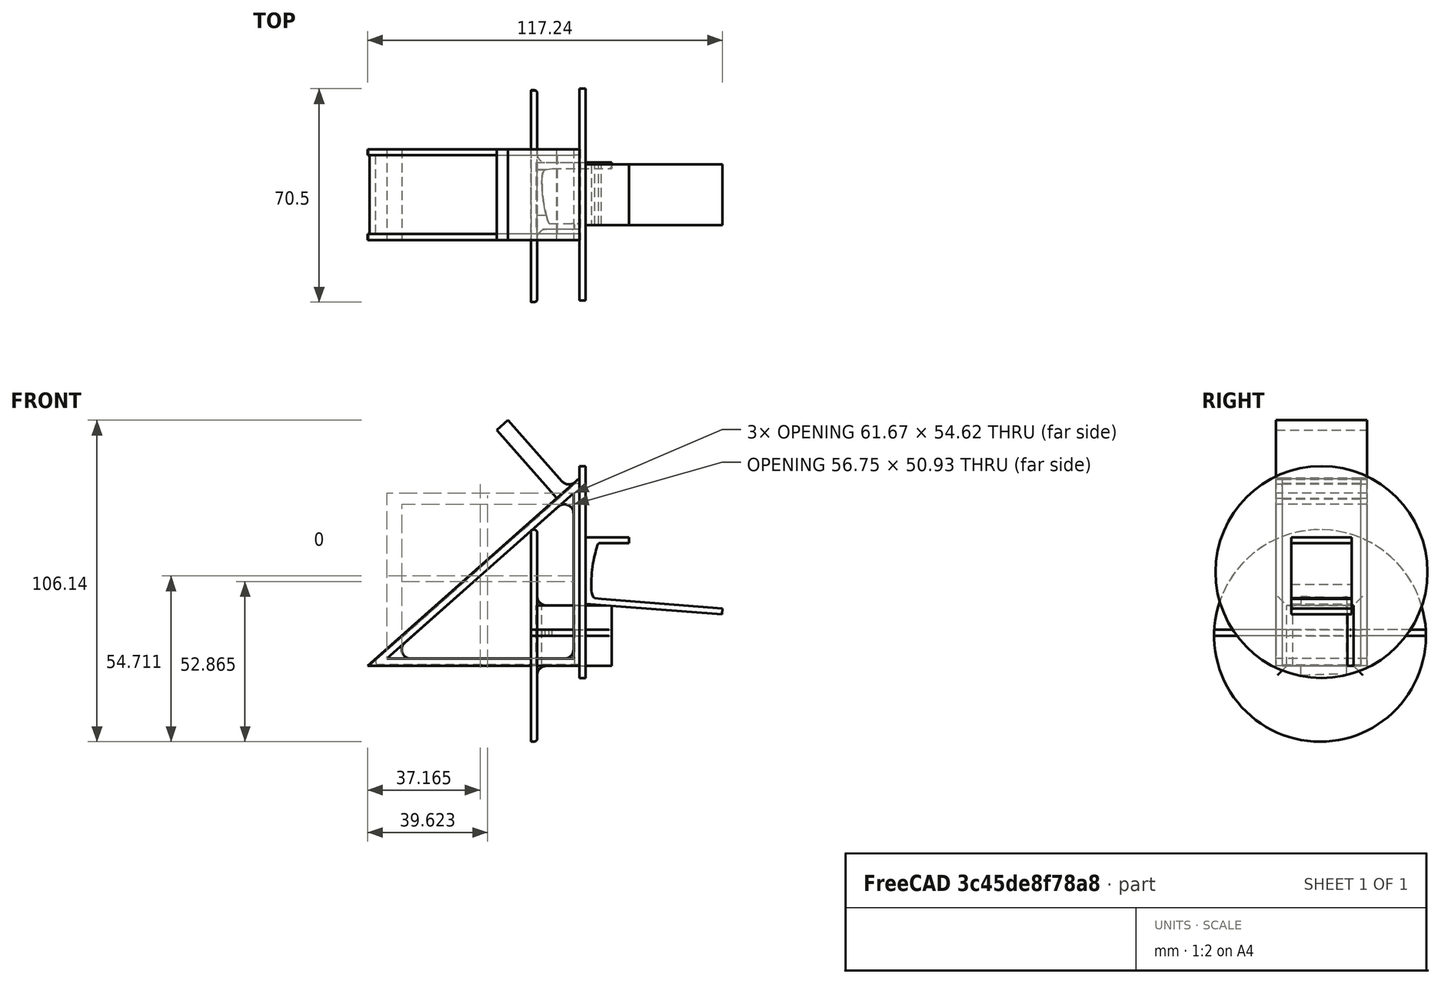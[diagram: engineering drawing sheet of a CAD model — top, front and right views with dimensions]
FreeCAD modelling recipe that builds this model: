
FCSTD DOCUMENT  (FreeCAD 0.20R29603 (Git))
Label: soporte
License: All rights reserved
LicenseURL: http://en.wikipedia.org/wiki/All_rights_reserved
objects: Sketcher::SketchObject×11, PartDesign::Body×8, PartDesign::Pad×6, PartDesign::Fillet×6, Mesh::Feature×4, Part::Feature×3, Part::Box×3, Part::Cut×3, Part::Fillet×3, Part::MultiFuse×3, PartDesign::Pocket×3, Part::Cylinder×2, Image::ImagePlane×1
note: 66 computed .brp shape members not serialized (recipe doc carries the construction recipe); baked Part::Feature solids carry a one-line shape summary decoded from their .brp

FEATURE [Image::ImagePlane] ImagePlane
  Placement = pos=(0,0,0) rot=(0,0,1;-0.034907rad)
  XSize = 116.767
  YSize = 87.5751
FEATURE [Sketcher::SketchObject] Sketch
  FullyConstrained = false
  MapMode = 5
  Support = -> [XY_Plane]
  sketch-geometry (21):
    g0: LineSegment StartX=-10 StartY=-9.49 StartZ=0 EndX=0 EndY=-9.49 EndZ=0
    g1: LineSegment StartX=0 StartY=-11.49 StartZ=0 EndX=-14.4197 EndY=-11.49 EndZ=0
    g2: LineSegment StartX=-11.2797 StartY=8.28 StartZ=0 EndX=-9.03969 EndY=8.58 EndZ=0
    g3: LineSegment StartX=-9.03969 StartY=8.58 StartZ=0 EndX=10.5803 EndY=8.58 EndZ=0
    g4-g10: Circle x7 (B-spline internal-alignment scaffolding for g11; pole/knot coordinates omitted)
    g11: BSplineCurve PolesCount=7 KnotsCount=5 Degree=3 IsPeriodic=0
    g12-g16: GeomPoint x5 (B-spline internal-alignment scaffolding for g11; pole/knot coordinates omitted)
    g17: LineSegment StartX=-14.4197 StartY=10.58 StartZ=0 EndX=-14.4197 EndY=-11.49 EndZ=0
    g18: LineSegment StartX=-14.4197 StartY=10.58 StartZ=0 EndX=10.5803 EndY=10.58 EndZ=0
    g19: LineSegment StartX=10.5803 StartY=10.58 StartZ=0 EndX=10.5803 EndY=8.58 EndZ=0
    g20: LineSegment StartX=0 StartY=-9.49 StartZ=0 EndX=0 EndY=-11.49 EndZ=0
  constraints (25):
    c: PointOnObject(g0,g-2)
    c: Horizontal(g0)
    c: PointOnObject(g1,g-2)
    c: Horizontal(g3)
    c: Coincident(g11,g2)
    c: Equal(g4, g5-g10) x6
    c: Coincident(g11,g0)
    c: InternalAlignment(g4-g10 -> g11) x7
    c: InternalAlignment(g12-g16 -> g11) x5
    c: DistanceY(g3,g18) = 2
    c: Coincident(g3,g2)
    c: DistanceX(g0,g0) = 10
    c: DistanceX(g17,g13) = 2
    c: Vertical(g17)
    c: Coincident(g1,g17)
    c: Coincident(g18,g17)
    c: Horizontal(g18)
    c: Horizontal(g1)
    c: DistanceY(g2,g2) = 0.3
    c: DistanceX(g3,g3) = 19.62
    c: DistanceX(g2,g2) = 2.24
    c: Coincident(g3,g19)
    c: Vertical(g20)
    c: Coincident(g20,g1)
    c: DistanceY(g20,g20) = 2
FEATURE [PartDesign::Pad] Pad
  Direction = (0,0,1)
  Length = 20
  Length2 = 10
  Profile = -> Sketch
  ReferenceAxis = -> Sketch [N_Axis]
  Type = 0
FEATURE [PartDesign::Body] Body
  Group = -> [Sketch,Pad]
  Origin = -> Origin
  Tip = -> Pad
FEATURE [Part::Feature] Body001
  shape: bbox 25 x 22.07 x 20 mm, 11 faces (baked)
FEATURE [Part::Box] Box  label="Cube"
  AttacherType = Attacher::AttachEngine3D
  Height = 21
  Length = 10
  Placement = pos=(-1.5,-16,0) rot=(0,0,1;0rad)
  Width = 12
FEATURE [Part::Cut] Cut
  Base = -> Body001
  Tool = -> Box
FEATURE [Part::Fillet] Fillet
  Base = -> Cut
  Edges = 4 edges r=0.9: [Edge9,Edge23,Edge24,Edge27]
FEATURE [Part::Cylinder] Cylinder
  Angle = 360
  AttacherType = Attacher::AttachEngine3D
  FirstAngle = 0
  Height = 2
  Placement = pos=(-16,-0.5,10) rot=(0,1,0;1.5708rad)
  Radius = 35
  SecondAngle = 0
FEATURE [Part::MultiFuse] Fusion
  Shapes = -> [Fillet,Cylinder]
FEATURE [Part::Fillet] Fillet001
  Base = -> Fusion
  Edges = 1 edges r=1: [Edge3]
FEATURE [Part::Fillet] Fillet002  label="pieza_tv"
  Base = -> Fillet001
  Edges = 4 edges r=3: [Edge6,Edge7,Edge8,Edge9]
FEATURE [Part::Feature] Fillet002001
  shape: bbox 26.58 x 75.77 x 75.77 mm, 30 faces (baked)
FEATURE [Part::Box] Box001  label="Cube001"
  AttacherType = Attacher::AttachEngine3D
  Height = 38
  Length = 42
  Placement = pos=(-21,-39,12) rot=(0,0,1;0rad)
  Width = 89
FEATURE [Part::Box] Box002  label="Cube002"
  AttacherType = Attacher::AttachEngine3D
  Height = 38
  Length = 42
  Placement = pos=(-21,-39,-28) rot=(0,0,1;0rad)
  Width = 89
FEATURE [Part::Cut] Cut001
  Base = -> Fillet002001
  Tool = -> Box001
FEATURE [Part::Cut] Cut002  label="prueba"
  Base = -> Cut001
  Tool = -> Box002
FEATURE [Mesh::Feature] Mesh  label="pieza"
FEATURE [Mesh::Feature] Mesh001  label="prueba001"
FEATURE [Sketcher::SketchObject] Sketch001
  FullyConstrained = true
  MapMode = 5
  Support = -> [XY_Plane001]
  sketch-geometry (1):
    g0: Circle CenterX=0 CenterY=0 CenterZ=0 NormalX=0 NormalY=0 NormalZ=1 AngleXU=0 Radius=15.5
  constraints (2):
    c: Coincident(g0,g-1)
    c: Diameter(g0) = 31
FEATURE [PartDesign::Body] Body002
  Group = -> [Sketch001]
  Origin = -> Origin001
FEATURE [PartDesign::Body] Body003
  Origin = -> Origin002
FEATURE [Sketcher::SketchObject] Sketch002
  FullyConstrained = false
  MapMode = 5
  Placement = pos=(0,0,0) rot=(1,0,0;1.5708rad)
  Support = -> [XZ_Plane003]
  sketch-geometry (7):
    g0: LineSegment StartX=0 StartY=0 StartZ=0 EndX=-70 EndY=0 EndZ=0
    g1: LineSegment StartX=-70 StartY=0 StartZ=0 EndX=0 EndY=62 EndZ=0
    g2: LineSegment StartX=0 StartY=62 StartZ=0 EndX=0 EndY=0 EndZ=0
    g3: LineSegment StartX=-2 StartY=2.4 StartZ=0 EndX=-63.6706 EndY=2.4 EndZ=0
    g4: LineSegment StartX=-63.6706 StartY=2.4 StartZ=0 EndX=-2 EndY=57.0225 EndZ=0
    g5: LineSegment StartX=-2 StartY=57.0225 StartZ=0 EndX=-2 EndY=2.4 EndZ=0
    g6: LineSegment StartX=-29.563 StartY=35.8157 StartZ=0 EndX=-27.9717 EndY=34.0191 EndZ=0
  constraints (20):
    c: Coincident(g-1,g0)
    c: PointOnObject(g0,g-1)
    c: Coincident(g0,g1)
    c: Coincident(g1,g2)
    c: Coincident(g2,g0)
    c: Vertical(g2)
    c: DistanceX(g0,g0) = 70
    c: DistanceY(g2,g2) = 62
    c: Horizontal(g3)
    c: Coincident(g3,g4)
    c: Coincident(g4,g5)
    c: Coincident(g5,g3)
    c: Vertical(g5)
    c: DistanceX(g3,g0) = 2
    c: DistanceY(g0,g3) = 2.4
    c: PointOnObject(g6,g1)
    c: Parallel(g1,g4)
    c: Perpendicular(g6,g1)
    c: PointOnObject(g6,g4)
    c: Distance(g6) = 2.4
FEATURE [PartDesign::Pad] Pad001
  Direction = (0,-1,2e-16)
  Length = 30
  Length2 = 10
  Midplane = true
  Placement = pos=(0,0,0) rot=(1,0,0;1.5708rad)
  Profile = -> Sketch002
  ReferenceAxis = -> Sketch002 [N_Axis]
  Type = 0
FEATURE [Sketcher::SketchObject] Sketch003
  ExternalGeometry = -> [Pad001]
  FullyConstrained = true
  MapMode = 5
  Placement = pos=(-30.7731,2.3e-14,34.7438) rot=(-0.35455,0,0.935037;3.14159rad)
  Support = -> [Pad001]
  sketch-geometry (4):
    g0: LineSegment StartX=-41.1082 StartY=13 StartZ=0 EndX=52.4012 EndY=13 EndZ=0
    g1: LineSegment StartX=52.4012 StartY=13 StartZ=0 EndX=52.4012 EndY=-13 EndZ=0
    g2: LineSegment StartX=52.4012 StartY=-13 StartZ=0 EndX=-41.1082 EndY=-13 EndZ=0
    g3: LineSegment StartX=-41.1082 StartY=-13 StartZ=0 EndX=-41.1082 EndY=13 EndZ=0
  constraints (11):
    c: Coincident(g0,g1)
    c: Coincident(g1,g2)
    c: Coincident(g2,g3)
    c: Coincident(g3,g0)
    c: Horizontal(g0)
    c: Horizontal(g2)
    c: Vertical(g1)
    c: Symmetric(g0,g2,g-1)
    c: DistanceY(g3,g3) = 26
    c: PointOnObject(g2,g-3)
    c: PointOnObject(g0,g-4)
FEATURE [PartDesign::Pocket] Pocket
  BaseFeature = -> Pad001
  Direction = (0.663035,-2e-16,-0.748588)
  Length = 0.37
  Length2 = 5
  Placement = pos=(0,0,0) rot=(1,0,0;1.5708rad)
  Profile = -> Sketch003
  ReferenceAxis = -> Sketch003 [N_Axis]
  Type = 0
FEATURE [Sketcher::SketchObject] Sketch004
  ExternalGeometry = -> [Pocket]
  FullyConstrained = true
  MapMode = 5
  Placement = pos=(0,0,-1e-16) rot=(1,0,0;3.14159rad)
  Support = -> [Pocket]
  sketch-geometry (4):
    g0: LineSegment StartX=-69.442 StartY=13 StartZ=0 EndX=0 EndY=13 EndZ=0
    g1: LineSegment StartX=0 StartY=13 StartZ=0 EndX=0 EndY=-13 EndZ=0
    g2: LineSegment StartX=0 StartY=-13 StartZ=0 EndX=-69.442 EndY=-13 EndZ=0
    g3: LineSegment StartX=-69.442 StartY=-13 StartZ=0 EndX=-69.442 EndY=13 EndZ=0
  constraints (10):
    c: Coincident(g0,g1)
    c: Coincident(g1,g2)
    c: Coincident(g2,g3)
    c: Coincident(g3,g0)
    c: Horizontal(g0)
    c: Horizontal(g2)
    c: Vertical(g1)
    c: Symmetric(g0,g2,g-1)
    c: Coincident(g0,g-4)
    c: PointOnObject(g0,g-2)
FEATURE [PartDesign::Pocket] Pocket001
  BaseFeature = -> Pocket
  Direction = (0,2e-16,1)
  Length = 0.37
  Length2 = 5
  Placement = pos=(0,0,0) rot=(1,0,0;1.5708rad)
  Profile = -> Sketch004
  ReferenceAxis = -> Sketch004 [N_Axis]
  Type = 0
FEATURE [PartDesign::Fillet] Fillet002002
  Base = -> Pocket001 [Edge27,Edge30,Edge28]
  BaseFeature = -> Pocket001
  Placement = pos=(0,0,0) rot=(1,0,0;1.5708rad)
  Radius = 3
  SupportTransform = false
  UseAllEdges = false
FEATURE [PartDesign::Fillet] Fillet002003
  Base = -> Fillet002002 [Edge26,Edge33]
  BaseFeature = -> Fillet002002
  Placement = pos=(0,0,0) rot=(1,0,0;1.5708rad)
  Radius = 0.2
  SupportTransform = false
  UseAllEdges = false
FEATURE [PartDesign::Fillet] Fillet002004
  Base = -> Fillet002003 [Edge21]
  BaseFeature = -> Fillet002003
  Placement = pos=(0,0,0) rot=(1,0,0;1.5708rad)
  Radius = 1
  SupportTransform = false
  UseAllEdges = false
FEATURE [PartDesign::Fillet] Fillet002005
  Base = -> Fillet002004 [Edge57,Edge40]
  BaseFeature = -> Fillet002004
  Placement = pos=(0,0,0) rot=(1,0,0;1.5708rad)
  Radius = 0.2
  SupportTransform = false
  UseAllEdges = false
FEATURE [PartDesign::Fillet] Fillet002006
  Base = -> Fillet002005 [Edge24]
  BaseFeature = -> Fillet002005
  Placement = pos=(0,0,0) rot=(1,0,0;1.5708rad)
  Radius = 1
  SupportTransform = false
  UseAllEdges = false
FEATURE [PartDesign::Body] Body004  label="triangulo"
  Group = -> [Sketch002,Pad001,Sketch003,Pocket,Sketch004,Pocket001,Fillet002002,Fillet002003,Fillet002004,Fillet002005,Fillet002006]
  Origin = -> Origin003
  Tip = -> Fillet002006
FEATURE [Mesh::Feature] Mesh002  label="triangulo001"
FEATURE [Part::Cylinder] Cylinder001  label="cilindro_grande"
  Angle = 360
  AttacherType = Attacher::AttachEngine3D
  FirstAngle = 0
  Height = 2
  Placement = pos=(-16.3,0,0) rot=(0,1,0;1.5708rad)
  Radius = 35
  SecondAngle = 0
FEATURE [Sketcher::SketchObject] Sketch005
  FullyConstrained = false
  MapMode = 5
  Support = -> [XY_Plane004]
  sketch-geometry (21):
    g0: LineSegment StartX=-10 StartY=-9.49 StartZ=0 EndX=0 EndY=-9.49 EndZ=0
    g1: LineSegment StartX=0 StartY=-11.49 StartZ=0 EndX=-14.42 EndY=-11.49 EndZ=0
    g2: LineSegment StartX=-11.28 StartY=8.59 StartZ=0 EndX=-9.04 EndY=8.89 EndZ=0
    g3: LineSegment StartX=-9.04 StartY=8.89 StartZ=0 EndX=30.9357 EndY=11.98 EndZ=0
    g4-g10: Circle x7 (B-spline internal-alignment scaffolding for g11; pole/knot coordinates omitted)
    g11: BSplineCurve PolesCount=7 KnotsCount=5 Degree=3 IsPeriodic=0
    g12-g16: GeomPoint x5 (B-spline internal-alignment scaffolding for g11; pole/knot coordinates omitted)
    g17: LineSegment StartX=-14.25 StartY=10.48 StartZ=0 EndX=-14.42 EndY=-11.49 EndZ=0
    g18: LineSegment StartX=-14.25 StartY=10.48 StartZ=0 EndX=30.7826 EndY=13.9609 EndZ=0
    g19: LineSegment StartX=0 StartY=-9.49 StartZ=0 EndX=0 EndY=-11.49 EndZ=0
    g20: LineSegment StartX=30.9357 StartY=11.98 StartZ=0 EndX=30.7826 EndY=13.9609 EndZ=0
  constraints (30):
    c: PointOnObject(g0,g-2)
    c: Horizontal(g0)
    c: PointOnObject(g1,g-2)
    c: Coincident(g11,g2)
    c: Equal(g4, g5-g10) x6
    c: Coincident(g11,g0)
    c: InternalAlignment(g4-g10 -> g11) x7
    c: InternalAlignment(g12-g16 -> g11) x5
    c: Horizontal(g1)
    c: Vertical(g19)
    c: Coincident(g19,g1)
    c: Parallel(g3,g18)
    c: DistanceY(g1,g0) = 2
    c: DistanceX(g0,g-1) = 10
    c: DistanceX(g1,g1) = 14.42
    c: DistanceY(g17,g17) = 21.97
    c: DistanceY(g-1,g2) = 8.89
    c: DistanceX(g2,g-1) = 9.04
    c: DistanceX(g2,g-1) = 11.28
    c: Coincident(g2,g3)
    c: Coincident(g17,g18)
    c: DistanceY(g-1,g17) = 10.48
    c: DistanceY(g-1,g2) = 8.59
    c: DistanceY(g-1,g3) = 11.98
    c: Angle(g18) = 0.0771436
    c: DistanceX(g17,g-1) = 14.25
    c: Coincident(g1,g17)
    c: Coincident(g3,g20)
    c: Perpendicular(g3,g20)
    c: Coincident(g18,g20)
FEATURE [PartDesign::Pad] Pad002
  Direction = (0,0,1)
  Length = 20
  Length2 = 10
  Midplane = true
  Profile = -> Sketch005
  ReferenceAxis = -> Sketch005 [N_Axis]
  Type = 0
FEATURE [PartDesign::Body] Body005  label="soporte_grande"
  Group = -> [Sketch005,Pad002]
  Origin = -> Origin004
  Tip = -> Pad002
FEATURE [Mesh::Feature] Mesh003  label="soporte_grande_test"
FEATURE [Sketcher::SketchObject] Sketch006
  ExternalGeometry = -> [Pad002]
  FullyConstrained = false
  MapMode = 5
  Placement = pos=(-14.3302,0.110885,0) rot=(-0.574372,0.578834,0.578834;4.18432rad)
  Support = -> [Pad002]
  sketch-geometry (2):
    g0: LineSegment StartX=-10.3694 StartY=10 StartZ=0 EndX=11.4689 EndY=-10 EndZ=0
    g1: LineSegment StartX=11.6012 StartY=9.89041 StartZ=0 EndX=-10.3694 EndY=-9.89756 EndZ=0
  constraints (4):
    c: Coincident(g0,g-4)
    c: PointOnObject(g0,g-6)
    c: PointOnObject(g1,g-5)
    c: PointOnObject(g1,g-4)
FEATURE [PartDesign::Body] Body006  label="triangulo002"
  Origin = -> Origin005
  Placement = pos=(-16.3,0,-31) rot=(0,0,1;0rad)
FEATURE [Sketcher::SketchObject] Sketch007
  FullyConstrained = false
  MapMode = 5
  Placement = pos=(0,0,0) rot=(1,0,0;1.5708rad)
  Support = -> [XZ_Plane005]
  sketch-geometry (7):
    g0: LineSegment StartX=0 StartY=0 StartZ=0 EndX=-70 EndY=0 EndZ=0
    g1: LineSegment StartX=-70 StartY=0 StartZ=0 EndX=0 EndY=62 EndZ=0
    g2: LineSegment StartX=0 StartY=62 StartZ=0 EndX=0 EndY=0 EndZ=0
    g3: LineSegment StartX=-2 StartY=2.4 StartZ=0 EndX=-63.6706 EndY=2.4 EndZ=0
    g4: LineSegment StartX=-63.6706 StartY=2.4 StartZ=0 EndX=-2 EndY=57.0225 EndZ=0
    g5: LineSegment StartX=-2 StartY=57.0225 StartZ=0 EndX=-2 EndY=2.4 EndZ=0
    g6: LineSegment StartX=-29.563 StartY=35.8157 StartZ=0 EndX=-27.9717 EndY=34.0191 EndZ=0
  constraints (20):
    c: Coincident(g-1,g0)
    c: PointOnObject(g0,g-1)
    c: Coincident(g0,g1)
    c: Coincident(g1,g2)
    c: Coincident(g2,g0)
    c: Vertical(g2)
    c: DistanceX(g0,g0) = 70
    c: DistanceY(g2,g2) = 62
    c: Horizontal(g3)
    c: Coincident(g3,g4)
    c: Coincident(g4,g5)
    c: Coincident(g5,g3)
    c: Vertical(g5)
    c: DistanceX(g3,g0) = 2
    c: DistanceY(g0,g3) = 2.4
    c: PointOnObject(g6,g1)
    c: Parallel(g1,g4)
    c: Perpendicular(g6,g1)
    c: PointOnObject(g6,g4)
    c: Distance(g6) = 2.4
FEATURE [PartDesign::Pad] Pad003
  Direction = (0,-1,2e-16)
  Length = 30
  Length2 = 10
  Midplane = true
  Placement = pos=(0,0,0) rot=(1,0,0;1.5708rad)
  Profile = -> Sketch007
  ReferenceAxis = -> Sketch007 [N_Axis]
  Type = 0
FEATURE [Sketcher::SketchObject] Sketch008
  ExternalGeometry = -> [Pad003]
  FullyConstrained = true
  MapMode = 5
  Placement = pos=(-30.7731,2.3e-14,34.7438) rot=(-0.35455,0,0.935037;3.14159rad)
  Support = -> [Pad003]
  sketch-geometry (4):
    g0: LineSegment StartX=-41.1082 StartY=13 StartZ=0 EndX=52.4012 EndY=13 EndZ=0
    g1: LineSegment StartX=52.4012 StartY=13 StartZ=0 EndX=52.4012 EndY=-13 EndZ=0
    g2: LineSegment StartX=52.4012 StartY=-13 StartZ=0 EndX=-41.1082 EndY=-13 EndZ=0
    g3: LineSegment StartX=-41.1082 StartY=-13 StartZ=0 EndX=-41.1082 EndY=13 EndZ=0
  constraints (11):
    c: Coincident(g0,g1)
    c: Coincident(g1,g2)
    c: Coincident(g2,g3)
    c: Coincident(g3,g0)
    c: Horizontal(g0)
    c: Horizontal(g2)
    c: Vertical(g1)
    c: Symmetric(g0,g2,g-1)
    c: DistanceY(g3,g3) = 26
    c: PointOnObject(g2,g-3)
    c: PointOnObject(g0,g-4)
FEATURE [PartDesign::Pocket] Pocket002
  Direction = (0.663035,-5e-16,-0.748588)
  Length = 0.37
  Length2 = 5
  Placement = pos=(0,0,0) rot=(1,0,0;1.5708rad)
  Profile = -> Sketch008
  ReferenceAxis = -> Sketch008 [N_Axis]
  Type = 0
FEATURE [Sketcher::SketchObject] Sketch010
  ExternalGeometry = -> [Pocket002]
  FullyConstrained = true
  MapMode = 5
  Placement = pos=(-30.5278,2.29e-14,34.4668) rot=(-0.35455,0,0.935037;3.14159rad)
  Support = -> [Pocket002]
  sketch-geometry (4):
    g0: LineSegment StartX=-41.1082 StartY=15 StartZ=0 EndX=-31.1082 EndY=15 EndZ=0
    g1: LineSegment StartX=-31.1082 StartY=15 StartZ=0 EndX=-31.1082 EndY=-15 EndZ=0
    g2: LineSegment StartX=-31.1082 StartY=-15 StartZ=0 EndX=-41.1082 EndY=-15 EndZ=0
    g3: LineSegment StartX=-41.1082 StartY=-15 StartZ=0 EndX=-41.1082 EndY=15 EndZ=0
  constraints (10):
    c: Coincident(g0,g1)
    c: Coincident(g1,g2)
    c: Coincident(g2,g3)
    c: Coincident(g3,g0)
    c: Horizontal(g0)
    c: Horizontal(g2)
    c: Vertical(g1)
    c: DistanceX(g2,g2) = 10
    c: Coincident(g0,g-4)
    c: Coincident(g2,g-5)
FEATURE [Part::Feature] Pocket002001
  Placement = pos=(0,0,0) rot=(1,0,0;1.5708rad)
  shape: bbox 70 x 30 x 62 mm, 12 faces (baked)
FEATURE [PartDesign::Pad] Pad004
  Direction = (-0.663035,5e-16,0.748588)
  Length = 0.37
  Length2 = 10
  Placement = pos=(0,0,0) rot=(1,0,0;1.5708rad)
  Profile = -> Sketch010
  ReferenceAxis = -> Sketch010 [N_Axis]
  Type = 0
FEATURE [PartDesign::Body] Body007
  Group = -> [Sketch010,Pad004]
  Origin = -> Origin006
  Tip = -> Pad004
FEATURE [Sketcher::SketchObject] Sketch011
  ExternalGeometry = -> [Pad004]
  FullyConstrained = true
  MapMode = 5
  Placement = pos=(-30.7731,2.88e-14,34.7438) rot=(-0.35455,0,0.935037;3.14159rad)
  Support = -> [Pad004]
  sketch-geometry (4):
    g0: LineSegment StartX=-36.1082 StartY=15 StartZ=0 EndX=-31.1082 EndY=15 EndZ=0
    g1: LineSegment StartX=-31.1082 StartY=15 StartZ=0 EndX=-31.1082 EndY=-15 EndZ=0
    g2: LineSegment StartX=-31.1082 StartY=-15 StartZ=0 EndX=-36.1082 EndY=-15 EndZ=0
    g3: LineSegment StartX=-36.1082 StartY=-15 StartZ=0 EndX=-36.1082 EndY=15 EndZ=0
  constraints (10):
    c: Coincident(g0,g1)
    c: Coincident(g1,g2)
    c: Coincident(g2,g3)
    c: Coincident(g3,g0)
    c: Horizontal(g0)
    c: Horizontal(g2)
    c: Vertical(g3)
    c: DistanceX(g0,g0) = 5
    c: Coincident(g0,g-4)
    c: Coincident(g1,g-5)
FEATURE [PartDesign::Pad] Pad005
  Direction = (-0.663035,6e-16,0.748588)
  Length = 30
  Length2 = 10
  Placement = pos=(0,0,0) rot=(1,0,0;1.5708rad)
  Profile = -> Sketch011
  ReferenceAxis = -> Sketch011 [N_Axis]
  Type = 0
FEATURE [PartDesign::Fillet] Fillet002007
  Base = -> Pad005 [Edge65,Edge62,Edge56]
  BaseFeature = -> Pad005
  Placement = pos=(0,0,0) rot=(1,0,0;1.5708rad)
  Radius = 3
  SupportTransform = false
  UseAllEdges = false
FEATURE [PartDesign::Body] Body008
  Group = -> [Sketch011,Pad005,Fillet002007]
  Origin = -> Origin007
  Tip = -> Fillet002007
FEATURE [Part::MultiFuse] Fusion001  label="triangulo_soporte"
  Shapes = -> [Body008,Pocket002]
FEATURE [Part::MultiFuse] Fusion002  label="soporte_tv_plano"
  Placement = pos=(16.3,0,31) rot=(1,0,0;4.71239rad)
  Shapes = -> [Body005,Cylinder001]
